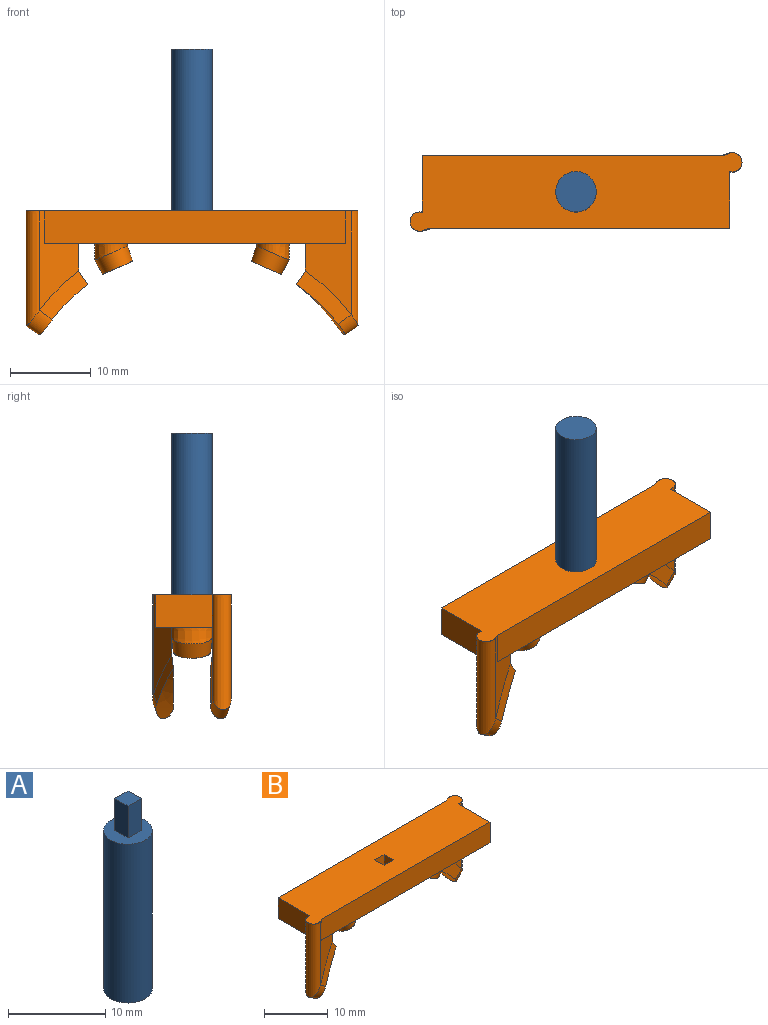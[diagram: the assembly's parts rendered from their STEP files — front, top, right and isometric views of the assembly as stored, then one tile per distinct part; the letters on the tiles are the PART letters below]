
ASSEMBLY  parts=2 mates=1
PART A: 8 faces, bbox 5x5x24 mm
  f0: plane 5x5mm, normal (0,0,1), area 16mm2, adj f1,f3,f4,f5,f6
  f1: cylinder r=2.5mm len=20mm, axis (0,0,-1), area 314.2mm2, adj f0,f2
  f2: plane 5x5mm, normal (0,0,-1), area 19.6mm2, adj f1
  f3: plane 4x1.9mm, normal (0,-1,0), area 7.6mm2, adj f0,f4,f6,f7
  f4: plane 4x1.9mm, normal (1,0,0), area 7.6mm2, adj f0,f3,f5,f7
  f5: plane 4x1.9mm, normal (0,1,0), area 7.6mm2, adj f0,f4,f6,f7
  f6: plane 4x1.9mm, normal (-1,0,0), area 7.6mm2, adj f0,f3,f5,f7
  f7: plane 1.9x1.9mm, normal (0,0,1), area 3.6mm2, adj f3,f4,f5,f6
PART B: 30 faces, bbox 41x9.7x15.3 mm
  f0: plane 38x9mm, normal (0,0,-1), area 295.2mm2, adj f4,f10,f11,f12,f18,f19,f20,f23
  f1: plane 41.04x9.71mm, normal (0,0,1), area 344.2mm2, adj f9,f10,f11,f12,f17,f18,f19,f20
  f2: bspline ~5x4.64mm, area 28.3mm2, adj f3,f4
  f3: sphere r=23mm, area 14.6mm2, adj f2
  f4: extruded ~5x4mm, area 17.1mm2, adj f0,f2
  f5: bspline ~3.22x3.11mm, area 10.3mm2, adj f6,f7,f8,f9
  f6: cone r=24.73mm half-angle=81.6deg, axis (-0.42,0.91,0), area 13.8mm2, adj f5,f7,f8,f10
  f7: cone r=24.87mm half-angle=84.3deg, axis (0,-1,0), area 15mm2, adj f5,f6,f8,f11
  f8: sphere r=23mm, area 10.3mm2, adj f5,f6,f7
  f9: extruded ~14.22x2.35mm, area 53.2mm2, adj f1,f5,f10,f11
  f10: plane 12.22x4.81mm, normal (0.42,-0.91,0), area 32mm2, adj f0,f1,f6,f9,f11,f12
  f11: plane 12.79x5.68mm, normal (0,1,0), area 35.9mm2, adj f0,f1,f7,f9,f10,f25
  f12: plane 37.29x4mm, normal (0,-1,0), area 149.2mm2, adj f0,f1,f10,f24
  f13: bspline ~3.22x3.1mm, area 10.3mm2, adj f14,f15,f16,f17
  f14: cone r=24.73mm half-angle=81.6deg, axis (0.42,-0.91,0), area 13.8mm2, adj f13,f15,f16,f18
  f15: cone r=24.87mm half-angle=84.3deg, axis (0,1,0), area 15mm2, adj f13,f14,f16,f19
  f16: sphere r=23mm, area 10.3mm2, adj f13,f14,f15
  f17: extruded ~14.22x2.35mm, area 53.2mm2, adj f1,f13,f18,f19
  f18: plane 12.22x4.81mm, normal (-0.42,0.91,0), area 32mm2, adj f0,f1,f14,f17,f19,f20
  f19: plane 12.79x5.68mm, normal (0,-1,0), area 35.9mm2, adj f0,f1,f15,f17,f18,f24
  f20: plane 37.29x4mm, normal (0,1,0), area 149.2mm2, adj f0,f1,f18,f25
  f21: bspline ~5x4.64mm, area 28.3mm2, adj f22,f23
  f22: sphere r=23mm, area 14.6mm2, adj f21
  f23: extruded ~5x4mm, area 17.1mm2, adj f0,f21
  f24: plane 7x4mm, normal (1,0,0), area 28mm2, adj f0,f1,f12,f19
  f25: plane 7x4mm, normal (-1,0,0), area 28mm2, adj f0,f1,f11,f20
  f26: plane 4x2mm, normal (0,1,0), area 8mm2, adj f0,f1,f27,f29
  f27: plane 4x2mm, normal (-1,0,0), area 8mm2, adj f0,f1,f26,f28
  f28: plane 4x2mm, normal (0,-1,0), area 8mm2, adj f0,f1,f27,f29
  f29: plane 4x2mm, normal (1,0,0), area 8mm2, adj f0,f1,f26,f28
PLACE A rot(axis=(1,0,0),180deg) t=(-1.3,0.56,20.19)mm
PLACE B t=(-1.3,0.56,-27.81)mm fixed
MATE fastened A.f1 <-> B.f1  axis (0,0,-1) through (-1.3,0.56,0.19)mm
